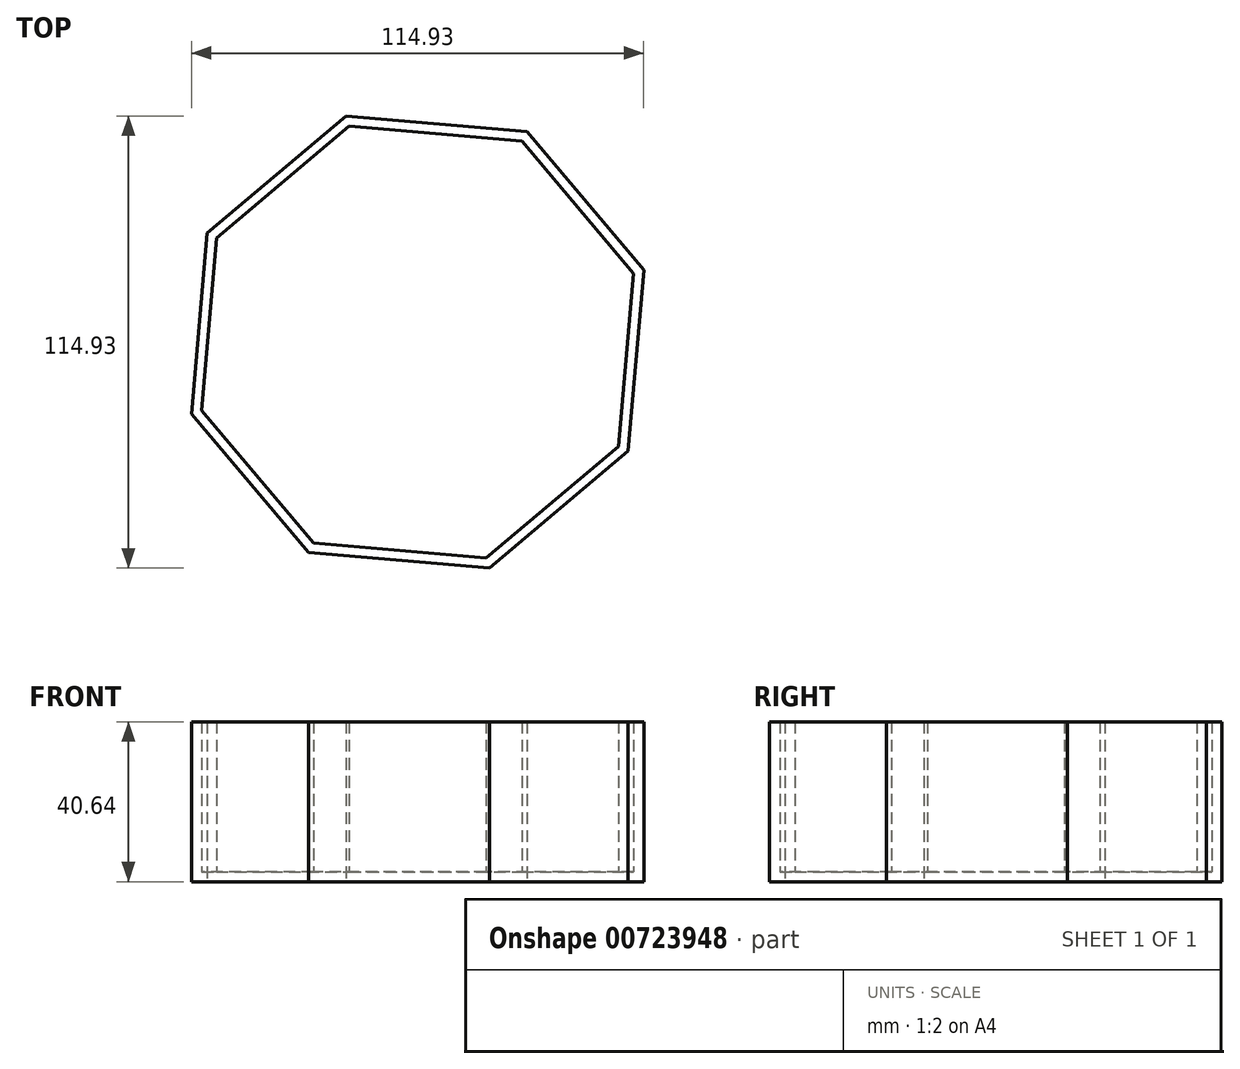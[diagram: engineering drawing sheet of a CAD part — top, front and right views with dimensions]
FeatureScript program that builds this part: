
annotation { "Feature Type Name" : "Feature", "Feature Type Description" : "" }
export const myFeature = defineFeature(function(context is Context, id is Id, definition is map)
    precondition{}
    {
        {
            var Q0;
            Q0=qCreatedBy(makeId("Top.planeOp"),FACE);
            var sketch = newSketch(context, id + "F0", { "sketchPlane" : qUnion([Q0])});
            skCircle(sketch, "E0.cCircle", {"center": v(-52.23, 17.98) * mm, "radius": 55.7 * mm, "construction": true});
            skLineSegment(sketch, "E0.0", {"start": v(-24.49, 71.5) * mm, "end": v(5.23, 36.2) * mm});
            skLineSegment(sketch, "E0.1", {"start": v(5.23, 36.2) * mm, "end": v(1.29, -9.76) * mm});
            skLineSegment(sketch, "E0.2", {"start": v(1.29, -9.76) * mm, "end": v(-34, -39.48) * mm});
            skLineSegment(sketch, "E0.3", {"start": v(-34, -39.48) * mm, "end": v(-79.98, -35.54) * mm});
            skLineSegment(sketch, "E0.4", {"start": v(-79.98, -35.54) * mm, "end": v(-109.7, -0.24) * mm});
            skLineSegment(sketch, "E0.5", {"start": v(-109.7, -0.24) * mm, "end": v(-105.75, 45.73) * mm});
            skLineSegment(sketch, "E0.6", {"start": v(-105.75, 45.73) * mm, "end": v(-70.46, 75.45) * mm});
            skLineSegment(sketch, "E0.7", {"start": v(-70.46, 75.45) * mm, "end": v(-24.49, 71.5) * mm});
            skPoint(sketch, "E0.0.midPoint", {"position": v(-9.63, 53.86) * mm});
            skSolve(sketch);
        }
        {
            var Q0;
            Q0=makeQuery(id+"F0.imprint","IMPRINT",FACE,{"disambiguationData":[TD([[makeQuery(id+"F0.imprint","IMPRINT",EDGE,{"derivedFrom":sQuery(id+"F0.wireOp",EDGE,"E0.0")}),-1.0]])]});
            extrude(context, id + "F1", {"entities" : qUnion([Q0]), "depth" : 40.64 * mm, "offsetDistance" : 25.4 * mm});
        }
        {
            var Q0;
            Q0=makeQuery(id+"F1.opExtrude","CAP_FACE",FACE,{"disambiguationData":[OSD([sQuery(id+"F0.wireOp",EDGE,"E0.0"),sQuery(id+"F0.wireOp",EDGE,"E0.1"),sQuery(id+"F0.wireOp",EDGE,"E0.2"),sQuery(id+"F0.wireOp",EDGE,"E0.3"),sQuery(id+"F0.wireOp",EDGE,"E0.4"),sQuery(id+"F0.wireOp",EDGE,"E0.5"),sQuery(id+"F0.wireOp",EDGE,"E0.6"),sQuery(id+"F0.wireOp",EDGE,"E0.7")])],"isStart":false});
            shell(context, id + "F2", {"entities" : qUnion([Q0]), "thickness" : 2.54 * mm});
        }
    });
